# Revit family: Hager-Vega-IP40-syst-NoHosted-CH-de
name_source: partatom
category: Electrical Equipment
units: mm (PartAtom-declared; Revit-internal decimal feet)

## family parameters
Always vertical = Yes
Cut with Voids When Loaded = No
Panel Configuration = Two Columns, Circuits Across
Part Type = Panelboard
Room Calculation Point = No
Round Connector Dimension = Use Diameter
Shared = No
Work Plane-Based = Yes

## types (8) — shared parameters
Default Elevation = 1219 mm
EF000003 - Montageart = EV000384 - Aufputz
EF000007 - Farbe = EV000202 - weiß
EF000008 - Breite = 400 mm  [stored 1.31234 ft]
EF000049 - Tiefe = 146 mm  [stored 0.479003 ft]
EF000116 - RAL-Nummer = 9010
EF000118 - Mit Montageplatte = No
EF000339 - Art der Abdeckung = EV004216 - Tür
EF001062 - EMV-Ausführung = No
EF001088 - Anbaumöglichkeit = Yes
EF001131 - Innentiefe = 120 mm
EF001134 - DIN-Schiene = Yes
EF001596 - Werkstoff des Gehäuses = EV000139 - Kunststoff
EF002950 - Breite in Teilungseinheiten = 18
EF004462 - Art der Schließung = EV000154 - sonstige
EF005474 - Schutzart (IP) = EV006415 - IP40
EF006306 - Mit Schloss = No
EF009212 - Ausführung Deckel = EV000116 - geschlossen
EF015776 - Erdungsklemmenblock = Yes
EF015777 - Neutralleiterklemmenblock = No
EF015941 - Signaldurchlassende Tür = Yes
HG000001 - Anzahl der Spalten = 1
HG000002 - Mit tür = Yes
HG000003 - Bereich = Vega
HG000005 - Dicke = 3 mm  [stored 0.00984252 ft]
HG000006 - Unterputz = No
HG000009 - Doppelflügeligen Tür = No
HG000010 - Asymmetrische Türen = No
HG000011 - Leere Reihen von unten = No
HG000017 - Distanz zwischen den Polen = 18 mm  [stored 0.0590551 ft]
Manufacturer = Hager
Type Comments = Vega
zero-valued in all types: EF000218 - Einbautiefe, EF000332 - Einbauhöhe, EF000846 - Einbaubreite, HG000007 - Anzahl der leeren Spalten, HG000008 - Anzahl der leeren Reihen

## per-type parameters (varying)
| type | EF000040 - Höhe | EF000266 - Anzahl der Reihen | EF006244 - Transparenter Deckel/Tür | HG000004 - Herstellerreferenz | Model |
| Aufputz IP40 B400 H325 T146 18 Teilungseinheiten - VB118B | 325 mm | 1 | No | VB118B | VB118B |
| Aufputz IP40 B400 H325 T146 18 Teilungseinheiten - VB118R | 325 mm | 1 | Yes | VB118R | VB118R |
| Aufputz IP40 B400 H475 T146 18 Teilungseinheiten - VB218B | 475 mm  [stored 1.5584 ft] | 2 | No | VB218B | VB218B |
| Aufputz IP40 B400 H475 T146 18 Teilungseinheiten - VB218R | 475 mm  [stored 1.5584 ft] | 2 | Yes | VB218R | VB218R |
| Aufputz IP40 B400 H625 T146 18 Teilungseinheiten - VB318B | 625 mm  [stored 2.05052 ft] | 3 | No | VB318B | VB318B |
| Aufputz IP40 B400 H625 T146 18 Teilungseinheiten - VB318R | 625 mm  [stored 2.05052 ft] | 3 | Yes | VB318R | VB318R |
| Aufputz IP40 B400 H775 T146 18 Teilungseinheiten - VB418B | 775 mm  [stored 2.54265 ft] | 4 | No | VB418B | VB418B |
| Aufputz IP40 B400 H775 T146 18 Teilungseinheiten - VB418R | 775 mm  [stored 2.54265 ft] | 4 | Yes | VB418R | VB418R |

note: [stored X ft] marks values corroborated as IEEE doubles in the binary element streams (Revit-internal decimal feet)

## geometry (parser evidence)
native form markers: Sweep x13
no freeform markers — native parametric forms only
